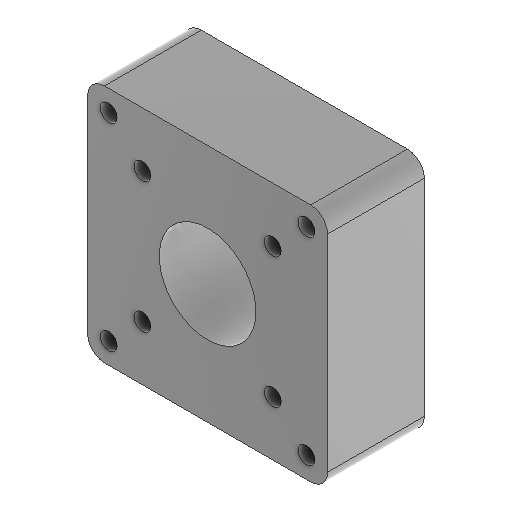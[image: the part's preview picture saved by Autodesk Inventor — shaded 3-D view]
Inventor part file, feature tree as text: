
AUTODESK INVENTOR PART (.ipt)
format: ipt  version: 2024.1 (Build 281209000, 209)  size: 153,088 bytes
history: native  units: mm
features: other x2, plane x1, extrude x1, sketch x1, reference x1
ambient origin geometry x8: Origin, YZ Plane, XZ Plane, XY Plane, X Axis, Y Axis, Z Axis, Center Point
bodies: Volumenkörper1 (feature_tree)
feature tree (6):
  plane  "Arbeitsebene1"
  extrude  "Extrusion1"  Depth=57.0mm
  sketch  "Skizze1"  dims[d0=57.0mm d1=57.0mm d2=4.0mm d3=47.0mm d4=47.0mm d5=4.0mm d6=4.0mm d7=4.0mm d8=4.0mm d9=23.0mm d10=0.0mm]
  reference  "Referenz1"
  other  "Assembly_Planktoscope_Uc2version.iam"
  other  "00_NEMA_17:1"
